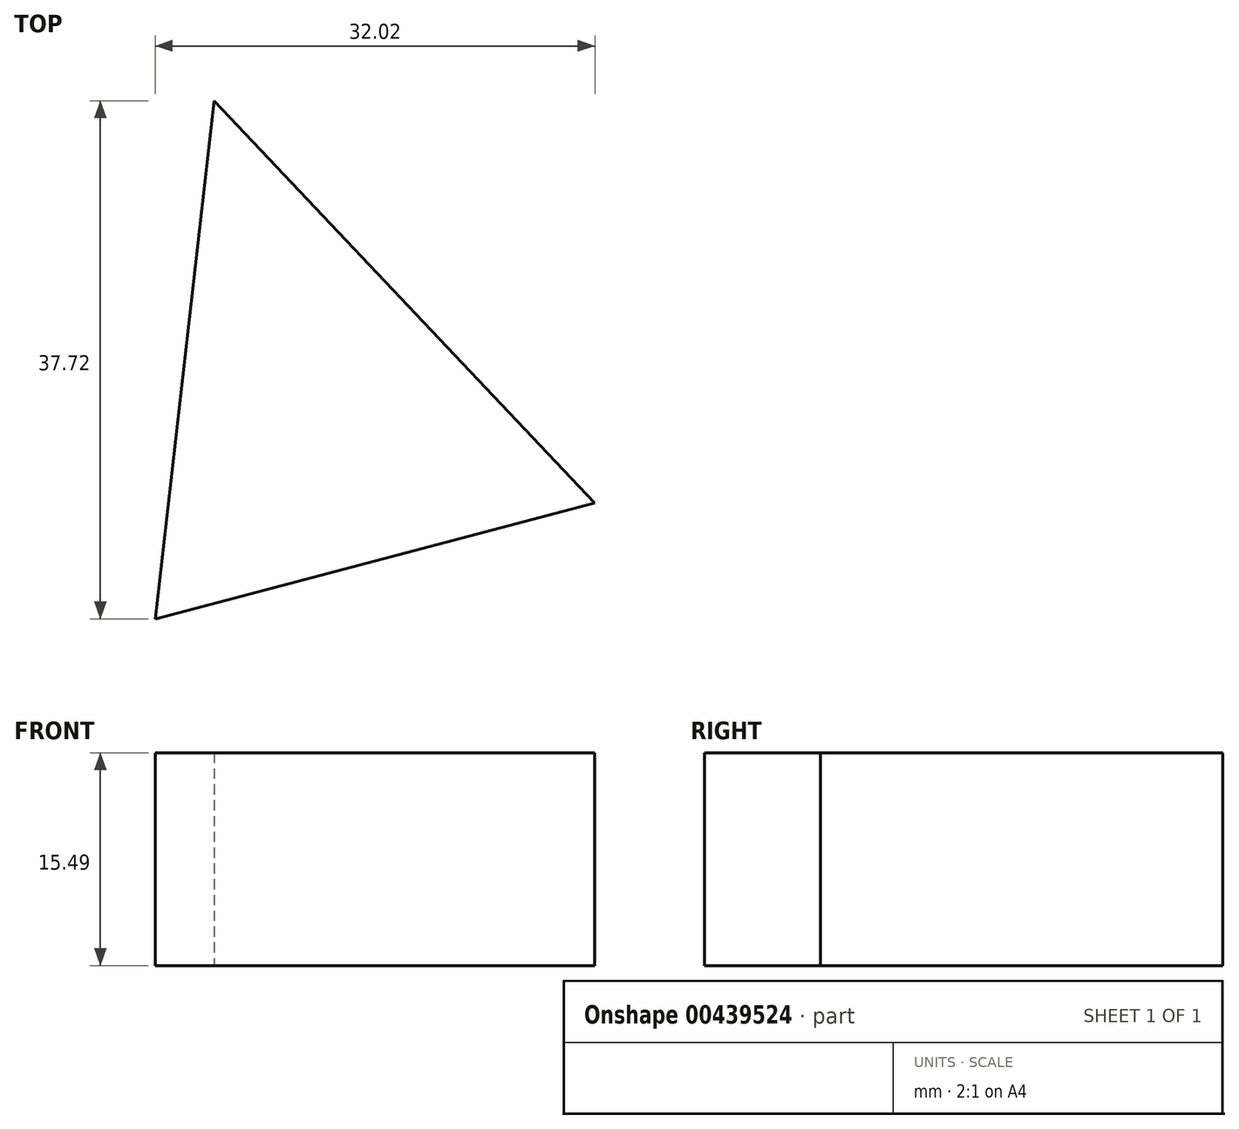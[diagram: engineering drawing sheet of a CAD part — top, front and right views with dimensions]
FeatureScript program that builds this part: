
annotation { "Feature Type Name" : "Feature", "Feature Type Description" : "" }
export const myFeature = defineFeature(function(context is Context, id is Id, definition is map)
    precondition{}
    {
        {
            var Q0;
            Q0=qCreatedBy(makeId("Top.planeOp"),FACE);
            var sketch = newSketch(context, id + "F0", { "sketchPlane" : qUnion([Q0])});
            skLineSegment(sketch, "E0", {"start": v(0, 3.88) * mm, "end": v(32.02, 12.3) * mm});
            skLineSegment(sketch, "E1", {"start": v(4.3, 41.6) * mm, "end": v(32.02, 12.3) * mm});
            skLineSegment(sketch, "E2", {"start": v(4.3, 41.6) * mm, "end": v(0, 3.88) * mm});
            skSolve(sketch);
        }
        {
            var Q0;
            Q0=makeQuery(id+"F0.imprint","IMPRINT",FACE,{"disambiguationData":[TD([[makeQuery(id+"F0.imprint","IMPRINT",EDGE,{"derivedFrom":sQuery(id+"F0.wireOp",EDGE,"E0")}),1.0]])]});
            extrude(context, id + "F1", {"entities" : qUnion([Q0]), "depth" : 15.5 * mm});
        }
    });
